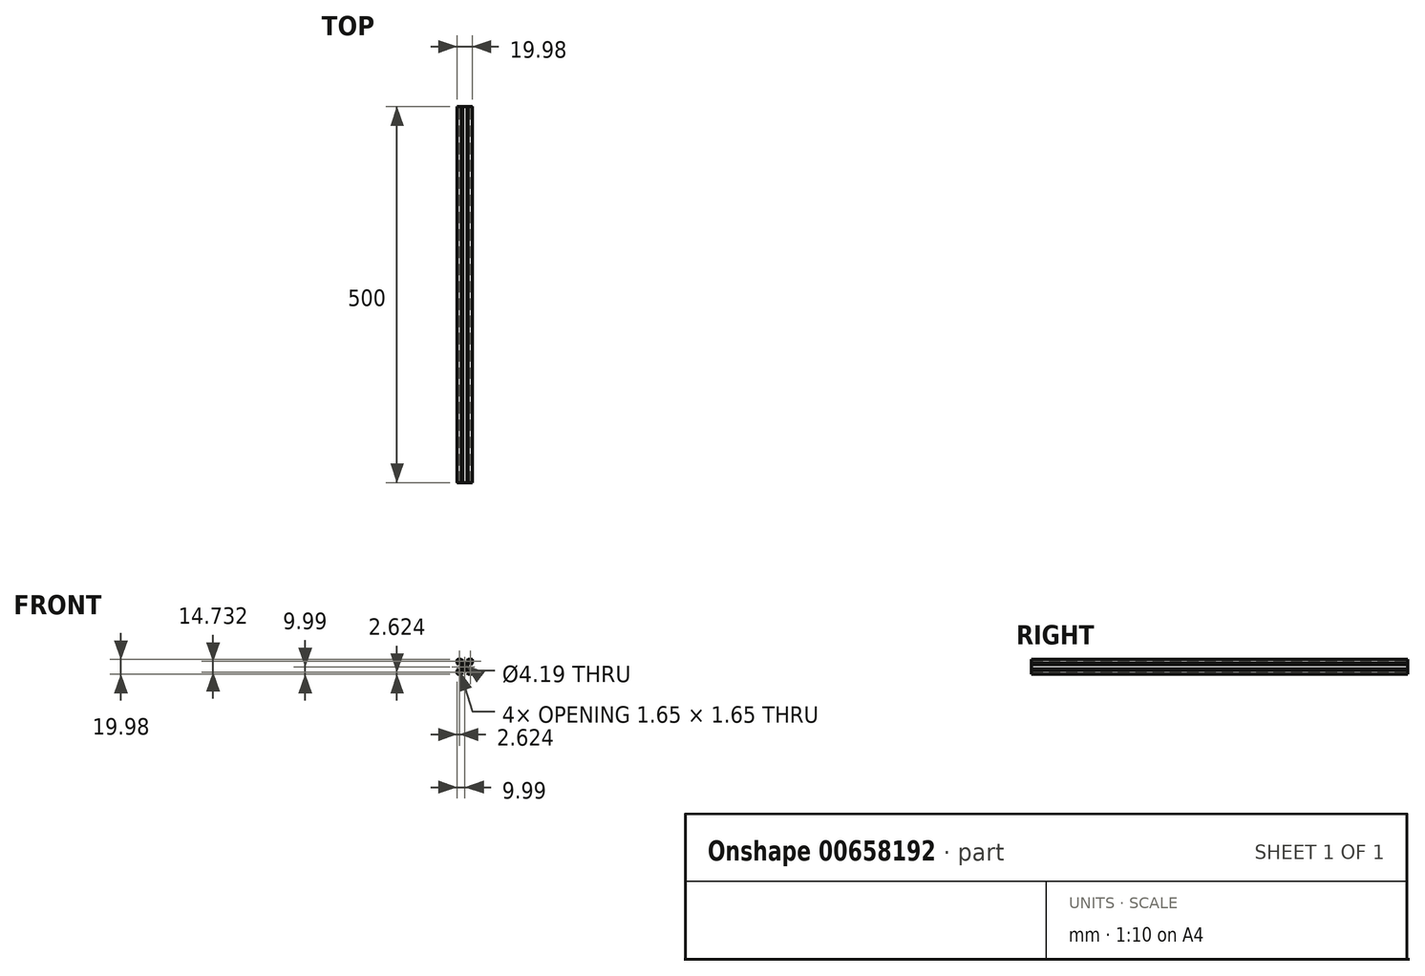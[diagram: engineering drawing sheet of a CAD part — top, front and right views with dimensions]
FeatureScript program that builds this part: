
annotation { "Feature Type Name" : "Feature", "Feature Type Description" : "" }
export const myFeature = defineFeature(function(context is Context, id is Id, definition is map)
    precondition{}
    {
        {
            var Q0;
            Q0=qCreatedBy(makeId("Front.planeOp"),FACE);
            var sketch = newSketch(context, id + "F0", { "sketchPlane" : qUnion([Q0])});
            skLineSegment(sketch, "E0.bottom", {"start": v(-9, 10) * mm, "end": v(-4.62, 10) * mm});
            skLineSegment(sketch, "E0.top", {"start": v(-9, -10) * mm, "end": v(-4.62, -10) * mm});
            skLineSegment(sketch, "E0.left", {"start": v(-10, 9) * mm, "end": v(-10, 4.62) * mm});
            skLineSegment(sketch, "E0.right", {"start": v(10, 9) * mm, "end": v(10, 4.62) * mm});
            skPoint(sketch, "E0.middle", {"position": v(0, 0) * mm});
            skPoint(sketch, "E1.visualSharp", {"position": v(10, 10) * mm});
            skArc(sketch, "E1.filletArc", {"start": v(10, 9) * mm, "mid": v(9.7, 9.7) * mm, "end": v(9, 10) * mm});
            skPoint(sketch, "E2.visualSharp", {"position": v(10, -10) * mm});
            skArc(sketch, "E2.filletArc", {"start": v(9, -10) * mm, "mid": v(9.7, -9.7) * mm, "end": v(10, -9) * mm});
            skPoint(sketch, "E3.visualSharp", {"position": v(-10, -10) * mm});
            skArc(sketch, "E3.filletArc", {"start": v(-10, -9) * mm, "mid": v(-9.7, -9.7) * mm, "end": v(-9, -10) * mm});
            skPoint(sketch, "E4.visualSharp", {"position": v(-10, 10) * mm});
            skArc(sketch, "E4.filletArc", {"start": v(-9, 10) * mm, "mid": v(-9.7, 9.7) * mm, "end": v(-10, 9) * mm});
            skCircle(sketch, "E5", {"center": v(0, 0) * mm, "radius": 2.1 * mm});
            skLineSegment(sketch, "E6.bottom", {"start": v(2.82, -3.9) * mm, "end": v(-2.82, -3.9) * mm});
            skLineSegment(sketch, "E6.top", {"start": v(2.82, 3.9) * mm, "end": v(-2.82, 3.9) * mm});
            skLineSegment(sketch, "E6.left", {"start": v(3.9, -2.82) * mm, "end": v(3.9, 2.82) * mm});
            skLineSegment(sketch, "E6.right", {"start": v(-3.9, -2.82) * mm, "end": v(-3.9, 2.82) * mm});
            skLineSegment(sketch, "E7.0", {"start": v(-6.54, 5.46) * mm, "end": v(-3.9, 2.82) * mm});
            skLineSegment(sketch, "E8.0", {"start": v(-5.46, 6.54) * mm, "end": v(-2.82, 3.9) * mm});
            skLineSegment(sketch, "E9.0", {"start": v(5.46, 6.54) * mm, "end": v(2.82, 3.9) * mm});
            skLineSegment(sketch, "E10.0", {"start": v(6.54, 5.46) * mm, "end": v(3.9, 2.82) * mm});
            skPoint(sketch, "E11.orphan", {"position": v(3.9, 3.9) * mm});
            skPoint(sketch, "E12.orphan", {"position": v(-3.9, 3.9) * mm});
            skPoint(sketch, "E13.orphan", {"position": v(-3.9, -3.9) * mm});
            skPoint(sketch, "E14.orphan", {"position": v(3.9, -3.9) * mm});
            skLineSegment(sketch, "E15.trimOffspring", {"start": v(3.9, -2.82) * mm, "end": v(6.54, -5.46) * mm});
            skLineSegment(sketch, "E16.trimOffspring", {"start": v(2.82, -3.9) * mm, "end": v(5.46, -6.54) * mm});
            skLineSegment(sketch, "E17.trimOffspring", {"start": v(-2.82, -3.9) * mm, "end": v(-5.46, -6.54) * mm});
            skLineSegment(sketch, "E18.trimOffspring", {"start": v(-3.9, -2.82) * mm, "end": v(-6.54, -5.46) * mm});
            skLineSegment(sketch, "E19", {"start": v(4.62, 10) * mm, "end": v(2.82, 8.2) * mm});
            skLineSegment(sketch, "E20", {"start": v(2.82, 8.2) * mm, "end": v(5.46, 8.2) * mm});
            skLineSegment(sketch, "E21", {"start": v(5.46, 8.2) * mm, "end": v(5.46, 6.54) * mm});
            skLineSegment(sketch, "E22.MirrorCS", {"start": v(-4.62, 10) * mm, "end": v(-2.82, 8.2) * mm});
            skLineSegment(sketch, "E23.MirrorCS", {"start": v(-2.82, 8.2) * mm, "end": v(-5.46, 8.2) * mm});
            skLineSegment(sketch, "E24.MirrorCS", {"start": v(-5.46, 8.2) * mm, "end": v(-5.46, 6.54) * mm});
            skLineSegment(sketch, "E25.MirrorCS", {"start": v(10, 4.62) * mm, "end": v(8.2, 2.82) * mm});
            skLineSegment(sketch, "E26.MirrorCS", {"start": v(8.2, 2.82) * mm, "end": v(8.2, 5.46) * mm});
            skLineSegment(sketch, "E27.MirrorCS", {"start": v(8.2, 5.46) * mm, "end": v(6.54, 5.46) * mm});
            skLineSegment(sketch, "E28.MirrorCS", {"start": v(-10, 4.62) * mm, "end": v(-8.2, 2.82) * mm});
            skLineSegment(sketch, "E29.MirrorCS", {"start": v(-8.2, 2.82) * mm, "end": v(-8.2, 5.46) * mm});
            skLineSegment(sketch, "E30.MirrorCS", {"start": v(-8.2, 5.46) * mm, "end": v(-6.54, 5.46) * mm});
            skLineSegment(sketch, "E31.MirrorCS", {"start": v(8.2, -5.46) * mm, "end": v(6.54, -5.46) * mm});
            skLineSegment(sketch, "E32.MirrorCS", {"start": v(8.2, -2.82) * mm, "end": v(8.2, -5.46) * mm});
            skLineSegment(sketch, "E33.MirrorCS", {"start": v(10, -4.62) * mm, "end": v(8.2, -2.82) * mm});
            skLineSegment(sketch, "E34.MirrorCS", {"start": v(-10, -4.62) * mm, "end": v(-8.2, -2.82) * mm});
            skLineSegment(sketch, "E35.MirrorCS", {"start": v(-8.2, -2.82) * mm, "end": v(-8.2, -5.46) * mm});
            skLineSegment(sketch, "E36.MirrorCS", {"start": v(-8.2, -5.46) * mm, "end": v(-6.54, -5.46) * mm});
            skLineSegment(sketch, "E37.MirrorCS", {"start": v(-5.46, -8.2) * mm, "end": v(-5.46, -6.54) * mm});
            skLineSegment(sketch, "E38.MirrorCS", {"start": v(-2.82, -8.2) * mm, "end": v(-5.46, -8.2) * mm});
            skLineSegment(sketch, "E39.MirrorCS", {"start": v(-4.62, -10) * mm, "end": v(-2.82, -8.2) * mm});
            skLineSegment(sketch, "E40.MirrorCS", {"start": v(4.62, -10) * mm, "end": v(2.82, -8.2) * mm});
            skLineSegment(sketch, "E41.MirrorCS", {"start": v(2.82, -8.2) * mm, "end": v(5.46, -8.2) * mm});
            skLineSegment(sketch, "E42.MirrorCS", {"start": v(5.46, -8.2) * mm, "end": v(5.46, -6.54) * mm});
            skLineSegment(sketch, "E43", {"start": v(-8.2, -8.04) * mm, "end": v(-8.2, -6.7) * mm});
            skLineSegment(sketch, "E44", {"start": v(-8.04, -8.2) * mm, "end": v(-6.7, -8.2) * mm});
            skLineSegment(sketch, "E45", {"start": v(-6.54, -8.04) * mm, "end": v(-6.54, -7.99) * mm});
            skLineSegment(sketch, "E46", {"start": v(-8.04, -6.54) * mm, "end": v(-7.99, -6.54) * mm});
            skLineSegment(sketch, "E47", {"start": v(-7.99, -6.54) * mm, "end": v(-6.54, -7.99) * mm});
            skPoint(sketch, "E48.visualSharp", {"position": v(-8.2, -8.2) * mm});
            skArc(sketch, "E48.filletArc", {"start": v(-8.2, -8.04) * mm, "mid": v(-8.15, -8.15) * mm, "end": v(-8.04, -8.2) * mm});
            skPoint(sketch, "E49.visualSharp", {"position": v(-6.54, -8.2) * mm});
            skArc(sketch, "E49.filletArc", {"start": v(-6.7, -8.2) * mm, "mid": v(-6.59, -8.15) * mm, "end": v(-6.54, -8.04) * mm});
            skPoint(sketch, "E50.visualSharp", {"position": v(-8.2, -6.54) * mm});
            skArc(sketch, "E50.filletArc", {"start": v(-8.04, -6.54) * mm, "mid": v(-8.15, -6.59) * mm, "end": v(-8.2, -6.7) * mm});
            skLineSegment(sketch, "E51.MirrorCS", {"start": v(8.2, -8.04) * mm, "end": v(8.2, -6.7) * mm});
            skArc(sketch, "E52.MirrorCS", {"start": v(8.2, -8.04) * mm, "mid": v(8.15, -8.15) * mm, "end": v(8.04, -8.2) * mm});
            skLineSegment(sketch, "E53.MirrorCS", {"start": v(8.04, -8.2) * mm, "end": v(6.7, -8.2) * mm});
            skArc(sketch, "E54.MirrorCS", {"start": v(6.7, -8.2) * mm, "mid": v(6.59, -8.15) * mm, "end": v(6.54, -8.04) * mm});
            skLineSegment(sketch, "E55.MirrorCS", {"start": v(6.54, -8.04) * mm, "end": v(6.54, -7.99) * mm});
            skLineSegment(sketch, "E56.MirrorCS", {"start": v(7.99, -6.54) * mm, "end": v(6.54, -7.99) * mm});
            skArc(sketch, "E57.MirrorCS", {"start": v(8.04, -6.54) * mm, "mid": v(8.15, -6.59) * mm, "end": v(8.2, -6.7) * mm});
            skLineSegment(sketch, "E58.MirrorCS", {"start": v(8.04, -6.54) * mm, "end": v(7.99, -6.54) * mm});
            skLineSegment(sketch, "E59.MirrorCS", {"start": v(8.04, 6.54) * mm, "end": v(7.99, 6.54) * mm});
            skLineSegment(sketch, "E60.MirrorCS", {"start": v(6.54, 8.04) * mm, "end": v(6.54, 7.99) * mm});
            skArc(sketch, "E61.MirrorCS", {"start": v(8.04, 6.54) * mm, "mid": v(8.15, 6.59) * mm, "end": v(8.2, 6.7) * mm});
            skArc(sketch, "E62.MirrorCS", {"start": v(6.7, 8.2) * mm, "mid": v(6.59, 8.15) * mm, "end": v(6.54, 8.04) * mm});
            skArc(sketch, "E63.MirrorCS", {"start": v(8.2, 8.04) * mm, "mid": v(8.15, 8.15) * mm, "end": v(8.04, 8.2) * mm});
            skLineSegment(sketch, "E64.MirrorCS", {"start": v(8.2, 8.04) * mm, "end": v(8.2, 6.7) * mm});
            skLineSegment(sketch, "E65.MirrorCS", {"start": v(8.04, 8.2) * mm, "end": v(6.7, 8.2) * mm});
            skLineSegment(sketch, "E66.MirrorCS", {"start": v(7.99, 6.54) * mm, "end": v(6.54, 7.99) * mm});
            skArc(sketch, "E67.MirrorCS", {"start": v(-8.04, 6.54) * mm, "mid": v(-8.15, 6.59) * mm, "end": v(-8.2, 6.7) * mm});
            skArc(sketch, "E68.MirrorCS", {"start": v(-6.7, 8.2) * mm, "mid": v(-6.59, 8.15) * mm, "end": v(-6.54, 8.04) * mm});
            skArc(sketch, "E69.MirrorCS", {"start": v(-8.2, 8.04) * mm, "mid": v(-8.15, 8.15) * mm, "end": v(-8.04, 8.2) * mm});
            skLineSegment(sketch, "E70.MirrorCS", {"start": v(-8.04, 6.54) * mm, "end": v(-7.99, 6.54) * mm});
            skLineSegment(sketch, "E71.MirrorCS", {"start": v(-6.54, 8.04) * mm, "end": v(-6.54, 7.99) * mm});
            skPoint(sketch, "E72.MirrorP", {"position": v(-8.2, 6.54) * mm});
            skPoint(sketch, "E73.MirrorP", {"position": v(-8.2, 8.2) * mm});
            skLineSegment(sketch, "E74.MirrorCS", {"start": v(-8.2, 8.04) * mm, "end": v(-8.2, 6.7) * mm});
            skLineSegment(sketch, "E75.MirrorCS", {"start": v(-7.99, 6.54) * mm, "end": v(-6.54, 7.99) * mm});
            skLineSegment(sketch, "E76.MirrorCS", {"start": v(-8.04, 8.2) * mm, "end": v(-6.7, 8.2) * mm});
            skPoint(sketch, "E77.MirrorP", {"position": v(-6.54, 8.2) * mm});
            skLineSegment(sketch, "E78.trimOffspring", {"start": v(10, -4.62) * mm, "end": v(10, -9) * mm});
            skLineSegment(sketch, "E79.trimOffspring", {"start": v(-10, -4.62) * mm, "end": v(-10, -9) * mm});
            skLineSegment(sketch, "E80.trimOffspring", {"start": v(4.62, -10) * mm, "end": v(9, -10) * mm});
            skLineSegment(sketch, "E81.trimOffspring", {"start": v(4.62, 10) * mm, "end": v(9, 10) * mm});
            skSolve(sketch);
        }
        {
            assignVariable(context, id + "F1", {"name" : "Length", "anyValue" : 500 * mm});
        }
        {
            var Q0;
            Q0=makeQuery(id+"F0.imprint","IMPRINT",FACE,{"disambiguationData":[TD([[makeQuery(id+"F0.imprint","IMPRINT",EDGE,{"derivedFrom":sQuery(id+"F0.wireOp",EDGE,"E0.bottom")}),-1.0]])]});
            extrude(context, id + "F2", {"entities" : qUnion([Q0]), "depth" : (getVariable(context, 'Length')), "offsetDistance" : 25.4 * mm});
        }
    });
